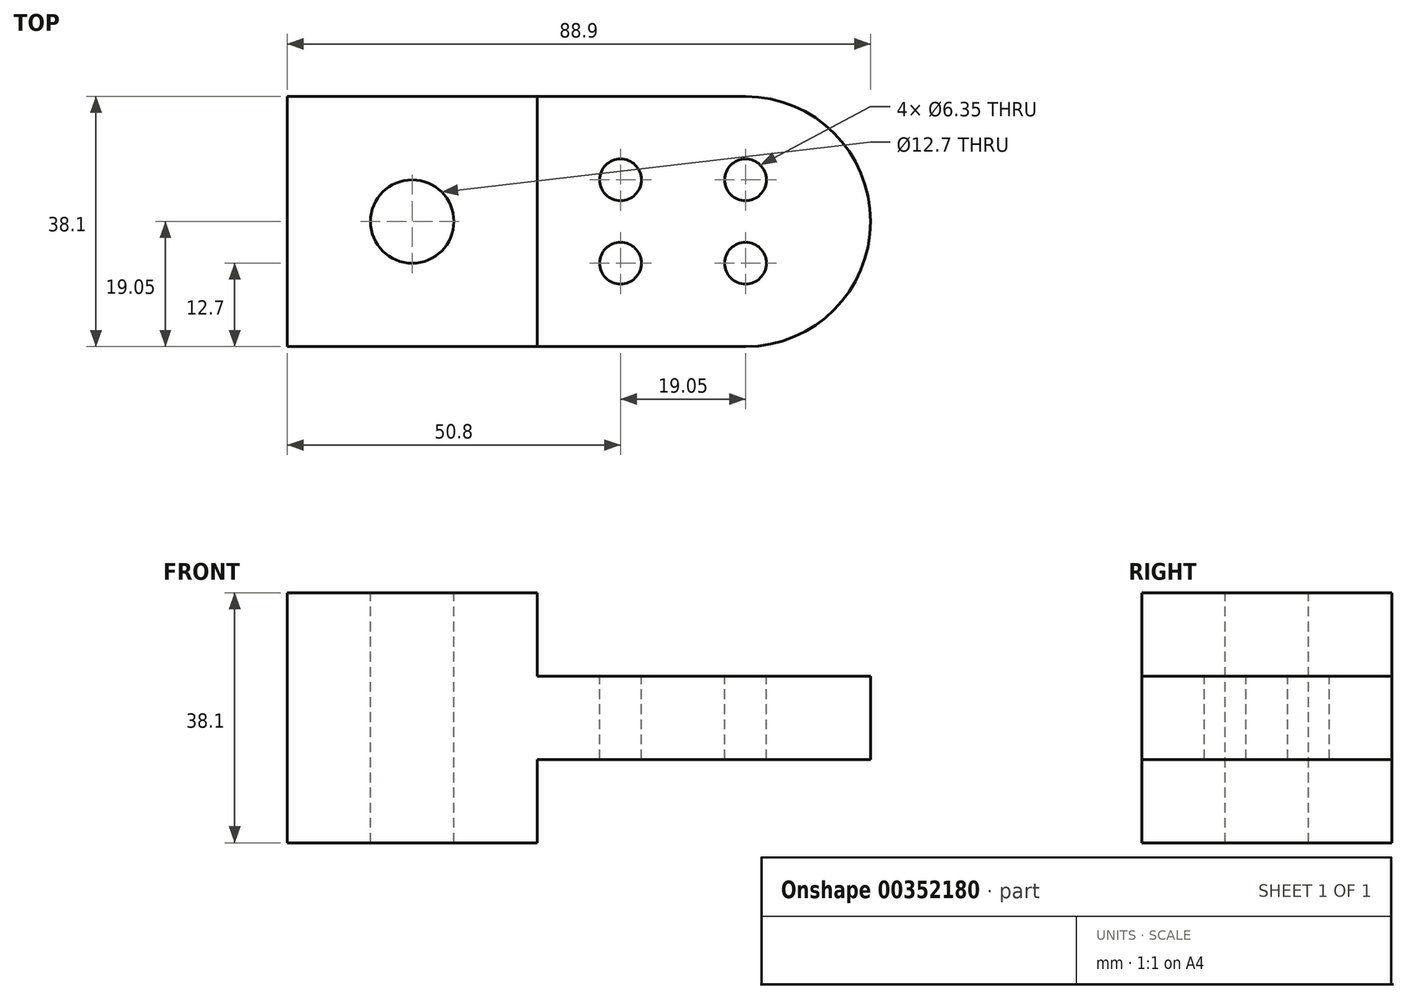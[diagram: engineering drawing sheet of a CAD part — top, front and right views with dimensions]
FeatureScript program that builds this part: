
annotation { "Feature Type Name" : "Feature", "Feature Type Description" : "" }
export const myFeature = defineFeature(function(context is Context, id is Id, definition is map)
    precondition{}
    {
        {
            var Q0;
            Q0=qCreatedBy(makeId("Top.planeOp"),FACE);
            var sketch = newSketch(context, id + "F0", { "sketchPlane" : qUnion([Q0])});
            skLineSegment(sketch, "E0.bottom", {"start": v(-19.05, 19.05) * mm, "end": v(19.05, 19.05) * mm});
            skLineSegment(sketch, "E0.top", {"start": v(-19.05, -19.05) * mm, "end": v(19.05, -19.05) * mm});
            skLineSegment(sketch, "E0.left", {"start": v(-19.05, 19.05) * mm, "end": v(-19.05, -19.05) * mm});
            skLineSegment(sketch, "E0.right", {"start": v(19.05, 19.05) * mm, "end": v(19.05, -19.05) * mm});
            skSolve(sketch);
        }
        {
            var Q0;
            Q0 = qSketchRegion(id + "F0", true);
            extrude(context, id + "F1", {"entities" : qUnion([Q0]), "endBound" : BoundingType.SYMMETRIC, "depth" : 38.1 * mm});
        }
        {
            var Q0;
            Q0=qCreatedBy(makeId("Top.planeOp"),FACE);
            var sketch = newSketch(context, id + "F2", { "sketchPlane" : qUnion([Q0])});
            skLineSegment(sketch, "E1", {"start": v(19.05, 19.05) * mm, "end": v(50.8, 19.05) * mm});
            skLineSegment(sketch, "E2", {"start": v(19.05, -19.05) * mm, "end": v(50.8, -19.05) * mm});
            skArc(sketch, "E3", {"start": v(50.8, -19.05) * mm, "mid": v(69.85, 0) * mm, "end": v(50.8, 19.05) * mm});
            skLineSegment(sketch, "E4", {"start": v(19.05, 19.05) * mm, "end": v(19.05, -19.05) * mm});
            skSolve(sketch);
        }
        {
            var Q0;
            Q0 = qSketchRegion(id + "F2", true);
            extrude(context, id + "F3", {"entities" : qUnion([Q0]), "operationType" : NewBodyOperationType.ADD, "endBound" : BoundingType.SYMMETRIC, "depth" : 12.7 * mm});
        }
        {
            var Q0;
            Q0=makeQuery(id+"F1.opExtrude","CAP_FACE",FACE,{"disambiguationData":[OSD([sQuery(id+"F0.wireOp",EDGE,"E0.bottom"),sQuery(id+"F0.wireOp",EDGE,"E0.top"),sQuery(id+"F0.wireOp",EDGE,"E0.left"),sQuery(id+"F0.wireOp",EDGE,"E0.right")])],"isStart":false});
            var sketch = newSketch(context, id + "F4", { "sketchPlane" : qUnion([Q0])});
            skCircle(sketch, "E5", {"center": v(0, 0) * mm, "radius": 6.35 * mm});
            skSolve(sketch);
        }
        {
            var Q0;
            Q0 = qSketchRegion(id + "F4", true);
            extrude(context, id + "F5", {"entities" : qUnion([Q0]), "operationType" : NewBodyOperationType.REMOVE, "endBound" : BoundingType.THROUGH_ALL, "oppositeDirection" : true, "depth" : 25.4 * mm});
        }
        {
            var Q0;
            Q0=makeQuery(id+"F3.opExtrude","CAP_FACE",FACE,{"disambiguationData":[OSD([sQuery(id+"F2.wireOp",EDGE,"E1"),sQuery(id+"F2.wireOp",EDGE,"E2"),sQuery(id+"F2.wireOp",EDGE,"E3"),sQuery(id+"F2.wireOp",EDGE,"E4")])],"isStart":false});
            var sketch = newSketch(context, id + "F6", { "sketchPlane" : qUnion([Q0])});
            skCircle(sketch, "E6", {"center": v(50.8, 6.35) * mm, "radius": 3.18 * mm});
            skCircle(sketch, "E7", {"center": v(50.8, -6.35) * mm, "radius": 3.18 * mm});
            skCircle(sketch, "E8", {"center": v(31.75, 6.35) * mm, "radius": 3.18 * mm});
            skCircle(sketch, "E9", {"center": v(31.75, -6.35) * mm, "radius": 3.18 * mm});
            skSolve(sketch);
        }
        {
            var Q0;
            Q0 = qSketchRegion(id + "F6", true);
            extrude(context, id + "F7", {"entities" : qUnion([Q0]), "operationType" : NewBodyOperationType.REMOVE, "endBound" : BoundingType.THROUGH_ALL, "oppositeDirection" : true, "depth" : 25.4 * mm});
        }
    });
